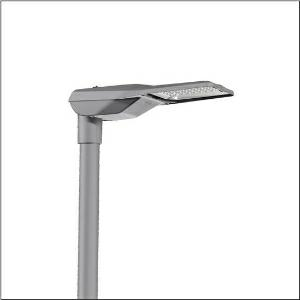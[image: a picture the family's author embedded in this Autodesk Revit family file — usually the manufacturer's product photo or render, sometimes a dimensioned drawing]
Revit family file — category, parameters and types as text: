
# Revit family: streetlight_sl_21_mini___st0_5a_5xe2b43s08hb_1e61
name_source: partatom
category: Lighting Fixtures
units: mm (PartAtom-declared; Revit-internal decimal feet)

## family parameters
Cut with Voids When Loaded = No
Host = Face
Light Source = No
Part Type = Normal
Room Calculation Point = No
Round Connector Dimension = Use Diameter
Shared = No

## types (1)
- --- (1 x LED, 9430 lm, 66 W, 4000K)
    Apparent Load = 66 VA
    CIE Flux Codes = 41 75 97 100 100
    Color Rendering = 70
    Color Temperature = 4000K
    Default Elevation = 1800 mm
    Description = Streetlight SL 21 mini, mast luminaire, primary light control with lens, of PMMA, primary optical cover: cover, of toughened safety glass, transparent, light distribution: ST0.5a, light emission: direct distribution, primary light characteristic: asymmetric, installation type: side-entry, post-top, LED, High Power LED, rated luminous flux: 9.430lm, luminous efficacy: 143lm/W, light colour: 740, colour temperature: 4000K, control gear: D4i, control: overheat protection, constant luminous flux control, time-dependent luminous flux control, flexible luminous flux parameterisation, pre-setting: logarithmic dimming characteristic, mains connection: 220..240V, AC, 50/60Hz, start of lifetime: 66W, end of service life: 69W, reduction: 30W, luminaire housing, of diecast aluminium, powder-coated, SITECO metallic grey (DB 702S), corrosivity category C5 high according to DIN EN ISO 12944, please order mast flange separately, inclination adjustable: 0°, 5°, 10°, 15°, sealing non-destructively replaceable, multi-level sealing system, length: 628mm, width: 235mm, height: 110mm, mast flange for spigot size: 42mm (side-entry): 5XC10008XM4, 60/48mm (side-entry/post-top): 5XC10108XM2, 76/60mm (side-entry/post-top): 5XC10108XM1, mounting height: 4..8m, Smart Interface above, protection rating (complete): IP66, insulation class (complete): insulation class II (safety insulation), certification: CE, ENEC, ENEC+, VDE, impact resistance: IK10, permissible operating ambient temperature for outdoor applications: -40..+50°C, standard-compliant lighting for roads and squares, packaging unit: 1 piece

Light Distribution: ST0.5a
    Height = 110 mm
    Lamp = 1 x LED
    Lamp Light Flux = 9430 lm
    Lamp Power = 66 W
    Lamp count = 1
    Length = 625 mm
    Luminous efficacy = 143 lm/W
    Manufacturer = Siteco
    ModVariant = No
    Model = 5XE2B43S08HB
    Number of Poles = 1
    OnlyDefault = Yes
    Power Factor = 1
    Product Name = Streetlight SL 21 mini | ST0.5a
    Product group = mast luminaire | pylon top
    ProductGroupID = 6100
    Protection Class = Protection class II
    Protection Degree = IP 66
    RLX_Detail_Level = 1
    RLX_Emergency_Light_Flux = 0 lm
    RLX_Emergency_Type = 0
    RLX_Emergency_Type_DB = No
    RlxData = <blob elided: 37093 chars, md5=96102e98>
    Socket = socket
    Standby Power = 0 W
    System Light Flux = 9430 lm
    System Power = 66 W
    Type Comments = factory setting: luminous flux: 100 % | dim-lin: 254 | 670 mA
    Type Image = l_1003515.jpg
    URL = http://relux.com
    VarID = @adj_188615
    Voltage = 0 V
    Weight = 0.00 kg
    Width = 234 mm

## geometry (parser evidence)
native form markers: Blend x4, Sweep x10
no freeform markers — native parametric forms only
